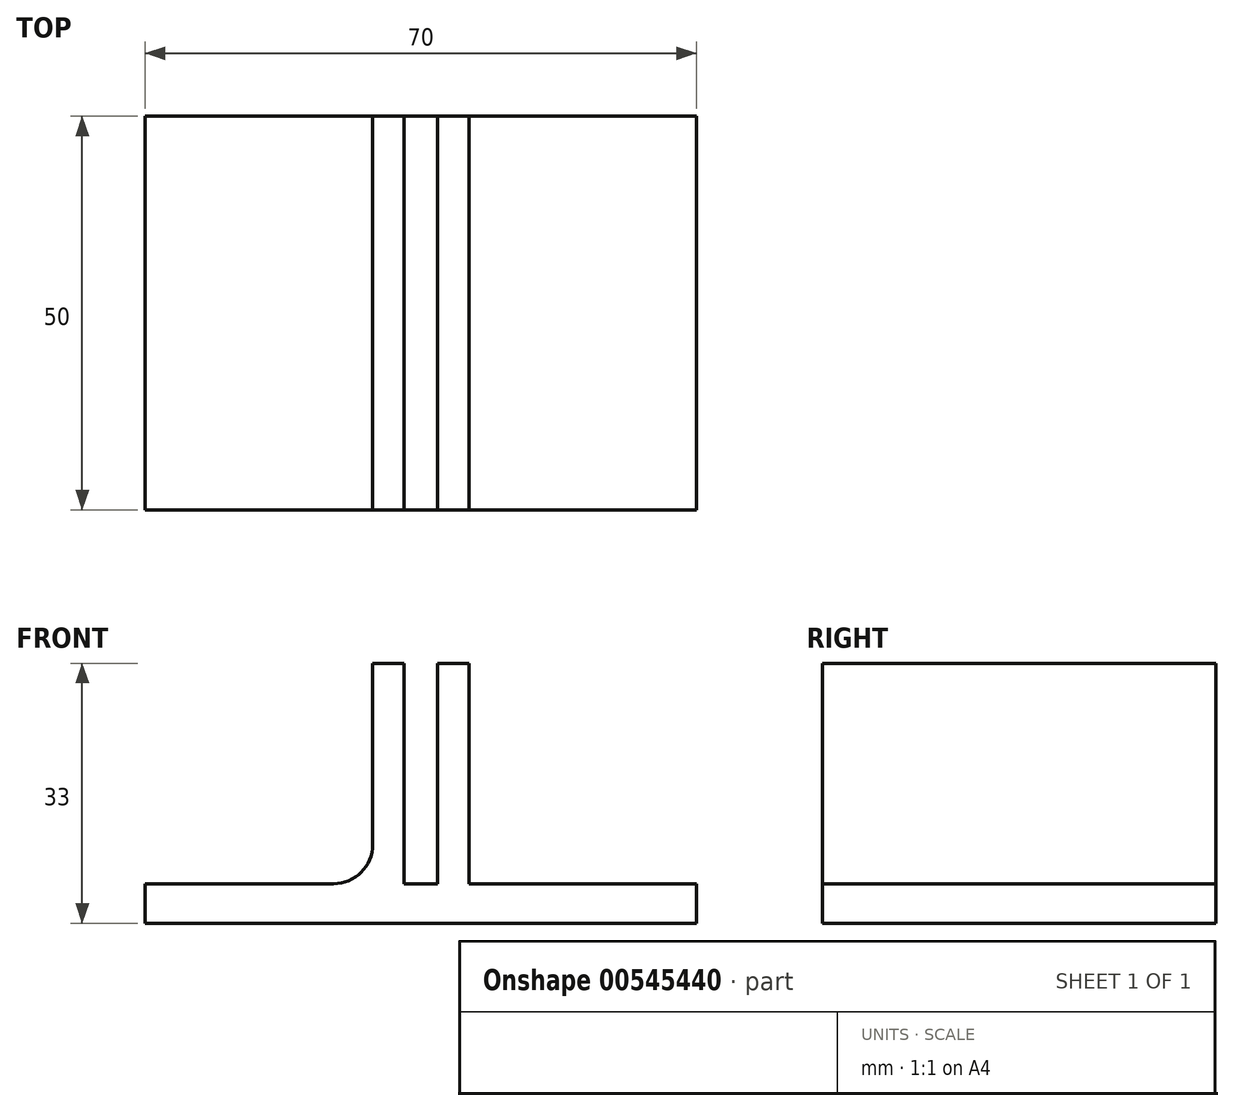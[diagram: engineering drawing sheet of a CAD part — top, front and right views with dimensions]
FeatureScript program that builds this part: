
annotation { "Feature Type Name" : "Feature", "Feature Type Description" : "" }
export const myFeature = defineFeature(function(context is Context, id is Id, definition is map)
    precondition{}
    {
        {
            var Q0;
            Q0=qCreatedBy(makeId("Top.planeOp"),FACE);
            var sketch = newSketch(context, id + "F0", { "sketchPlane" : qUnion([Q0])});
            skLineSegment(sketch, "E0.bottom", {"start": v(35, -25) * mm, "end": v(-35, -25) * mm});
            skLineSegment(sketch, "E0.top", {"start": v(35, 25) * mm, "end": v(-35, 25) * mm});
            skLineSegment(sketch, "E0.left", {"start": v(35, -25) * mm, "end": v(35, 25) * mm});
            skLineSegment(sketch, "E0.right", {"start": v(-35, -25) * mm, "end": v(-35, 25) * mm});
            skPoint(sketch, "E0.middle", {"position": v(0, 0) * mm});
            skSolve(sketch);
        }
        {
            var Q0;
            Q0 = qSketchRegion(id + "F0", true);
            extrude(context, id + "F1", {"entities" : qUnion([Q0]), "depth" : 5 * mm, "offsetDistance" : 25 * mm});
        }
        {
            var Q0;
            Q0=makeQuery(id+"F1.opExtrude","CAP_FACE",FACE,{"disambiguationData":[OSD([sQuery(id+"F0.wireOp",EDGE,"E0.bottom"),sQuery(id+"F0.wireOp",EDGE,"E0.top"),sQuery(id+"F0.wireOp",EDGE,"E0.left"),sQuery(id+"F0.wireOp",EDGE,"E0.right")])],"isStart":false});
            var sketch = newSketch(context, id + "F2", { "sketchPlane" : qUnion([Q0])});
            skLineSegment(sketch, "E1.bottom", {"start": v(-2.1, -25) * mm, "end": v(2.1, -25) * mm});
            skLineSegment(sketch, "E1.top", {"start": v(-2.1, 25) * mm, "end": v(2.1, 25) * mm});
            skLineSegment(sketch, "E1.left", {"start": v(-2.1, -25) * mm, "end": v(-2.1, 25) * mm});
            skLineSegment(sketch, "E1.right", {"start": v(2.1, -25) * mm, "end": v(2.1, 25) * mm});
            skPoint(sketch, "E1.middle", {"position": v(0, 0) * mm});
            skLineSegment(sketch, "E2.bottom", {"start": v(6.1, -25) * mm, "end": v(-6.1, -25) * mm});
            skLineSegment(sketch, "E2.top", {"start": v(6.1, 25) * mm, "end": v(-6.1, 25) * mm});
            skLineSegment(sketch, "E2.left", {"start": v(6.1, -25) * mm, "end": v(6.1, 25) * mm});
            skLineSegment(sketch, "E2.right", {"start": v(-6.1, -25) * mm, "end": v(-6.1, 25) * mm});
            skLineSegment(sketch, "E3", {"start": v(2.1, 0) * mm, "end": v(6.1, 0) * mm, "construction": true});
            skLineSegment(sketch, "E4", {"start": v(-2.1, 0) * mm, "end": v(2.1, 0) * mm, "construction": true});
            skSolve(sketch);
        }
        {
            var Q0;
            {var subQ0=sQuery(id+"F2.wireOp",EDGE,"E1.left");Q0=makeQuery(id+"F2.imprint","IMPRINT",FACE,{"disambiguationData":[TD([[makeQuery(id+"F2.imprint","IMPRINT",EDGE,{"derivedFrom":subQ0}),1.0]])]});}
            var Q1;
            {var subQ0=sQuery(id+"F2.wireOp",EDGE,"E1.right");Q1=makeQuery(id+"F2.imprint","IMPRINT",FACE,{"disambiguationData":[TD([[makeQuery(id+"F2.imprint","IMPRINT",EDGE,{"derivedFrom":subQ0}),-1.0]])]});}
            extrude(context, id + "F3", {"entities" : qUnion([Q0, Q1]), "operationType" : NewBodyOperationType.ADD, "depth" : 28 * mm, "offsetDistance" : 25 * mm});
        }
        {
            var Q0;
            Q0=makeQuery(id+"F3.opExtrude","CAP_EDGE",EDGE,{"disambiguationData":[OSD([sQuery(id+"F2.wireOp",EDGE,"E2.right")])],"isStart":true});
            var Q1;
            Q1=makeQuery(id+"F3.opExtrude","CAP_EDGE",EDGE,{"disambiguationData":[OSD([sQuery(id+"F2.wireOp",EDGE,"E2.left")])],"isStart":true});
            fillet(context, id + "F4", {"entities" : qUnion([Q0, Q1]), "radius" : 5 * mm, "tangentPropagation" : true, "allowEdgeOverflow" : false});
        }
    });
